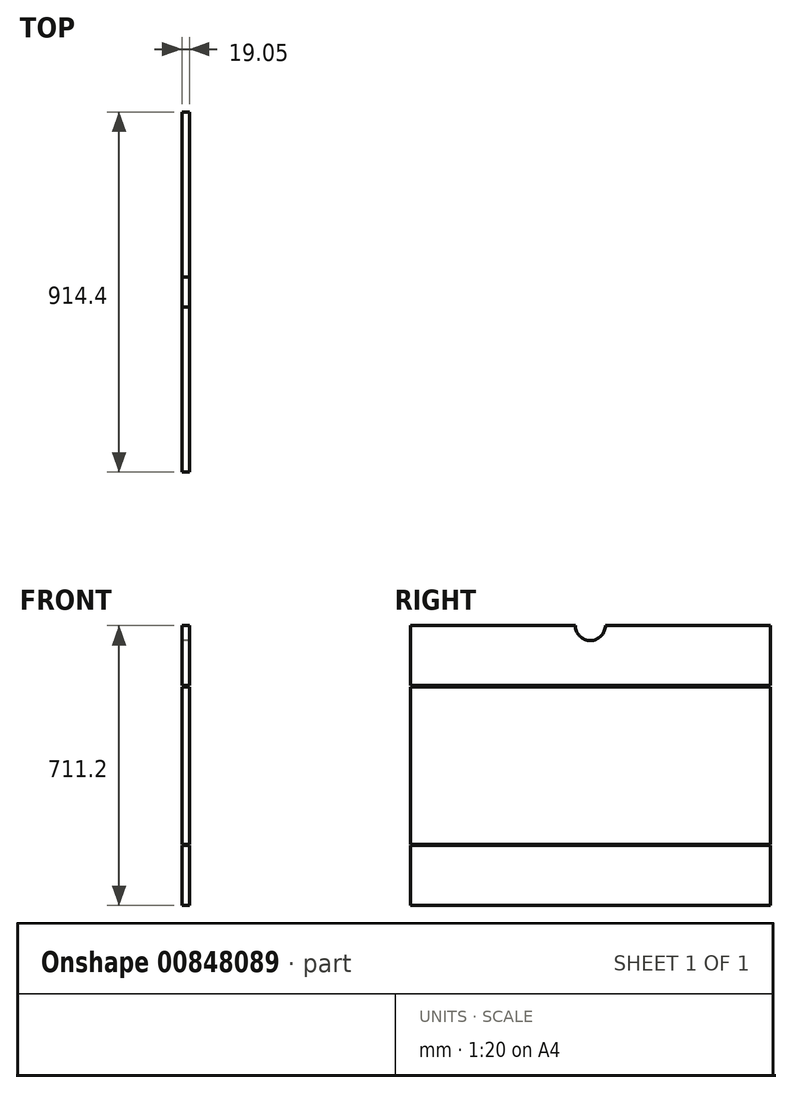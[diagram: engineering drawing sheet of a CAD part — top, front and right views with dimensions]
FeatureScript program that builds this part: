
annotation { "Feature Type Name" : "Feature", "Feature Type Description" : "" }
export const myFeature = defineFeature(function(context is Context, id is Id, definition is map)
    precondition{}
    {
        {
            var Q0;
            Q0=qCreatedBy(makeId("Right.planeOp"),FACE);
            var sketch = newSketch(context, id + "F0", { "sketchPlane" : qUnion([Q0])});
            skLineSegment(sketch, "E0.bottom", {"start": v(457.2, 355.6) * mm, "end": v(-457.2, 355.6) * mm});
            skLineSegment(sketch, "E0.top", {"start": v(457.2, -355.6) * mm, "end": v(-457.2, -355.6) * mm});
            skLineSegment(sketch, "E0.left", {"start": v(457.2, 355.6) * mm, "end": v(457.2, -355.6) * mm});
            skLineSegment(sketch, "E0.right", {"start": v(-457.2, 355.6) * mm, "end": v(-457.2, -355.6) * mm});
            skPoint(sketch, "E0.middle", {"position": v(0, 0) * mm});
            skCircle(sketch, "E1", {"center": v(0, 355.6) * mm, "radius": 38.1 * mm});
            skSolve(sketch);
        }
        {
            var Q0;
            Q0=makeQuery(id+"F0.imprint","IMPRINT",FACE,{"disambiguationData":[TD([[makeQuery(id+"F0.imprint","IMPRINT",EDGE,{"derivedFrom":sQuery(id+"F0.wireOp",EDGE,"E0.top")}),-1.0]])]});
            extrude(context, id + "F1", {"entities" : qUnion([Q0]), "depth" : 19.05 * mm, "offsetDistance" : 25.4 * mm});
        }
        {
            var Q0;
            Q0=makeQuery(id+"F1.opExtrude","CAP_FACE",FACE,{"disambiguationData":[OSD([sQuery(id+"F0.wireOp",EDGE,"E0.bottom"),sQuery(id+"F0.wireOp",EDGE,"E0.top"),sQuery(id+"F0.wireOp",EDGE,"E0.left"),sQuery(id+"F0.wireOp",EDGE,"E0.right"),sQuery(id+"F0.wireOp",EDGE,"E1")])],"isStart":false});
            var sketch = newSketch(context, id + "F2", { "sketchPlane" : qUnion([Q0])});
            skLineSegment(sketch, "E2.bottom", {"start": v(-457.2, 355.6) * mm, "end": v(457.2, 355.6) * mm});
            skLineSegment(sketch, "E2.top", {"start": v(-457.2, 203.2) * mm, "end": v(457.2, 203.2) * mm});
            skLineSegment(sketch, "E2.left", {"start": v(-457.2, 355.6) * mm, "end": v(-457.2, 203.2) * mm});
            skLineSegment(sketch, "E2.right", {"start": v(457.2, 355.6) * mm, "end": v(457.2, 203.2) * mm});
            skLineSegment(sketch, "E3.bottom", {"start": v(-457.2, -355.6) * mm, "end": v(457.2, -355.6) * mm});
            skLineSegment(sketch, "E3.top", {"start": v(-457.2, -203.2) * mm, "end": v(457.2, -203.2) * mm});
            skLineSegment(sketch, "E3.left", {"start": v(-457.2, -355.6) * mm, "end": v(-457.2, -203.2) * mm});
            skLineSegment(sketch, "E3.right", {"start": v(457.2, -355.6) * mm, "end": v(457.2, -203.2) * mm});
            skLineSegment(sketch, "E4.top", {"start": v(-457.2, 200.02) * mm, "end": v(457.2, 200.02) * mm});
            skLineSegment(sketch, "E4.left", {"start": v(-457.2, 203.2) * mm, "end": v(-457.2, 200.02) * mm});
            skLineSegment(sketch, "E4.right", {"start": v(457.2, 203.2) * mm, "end": v(457.2, 200.02) * mm});
            skLineSegment(sketch, "E5.top", {"start": v(-457.2, -200.03) * mm, "end": v(457.2, -200.03) * mm});
            skLineSegment(sketch, "E5.left", {"start": v(-457.2, -203.2) * mm, "end": v(-457.2, -200.03) * mm});
            skLineSegment(sketch, "E5.right", {"start": v(457.2, -203.2) * mm, "end": v(457.2, -200.03) * mm});
            skSolve(sketch);
        }
        {
            var Q0;
            Q0=makeQuery(id+"F2.imprint","IMPRINT",FACE,{"disambiguationData":[TD([[makeQuery(id+"F2.imprint","IMPRINT",EDGE,{"derivedFrom":sQuery(id+"F2.wireOp",EDGE,"E2.top")}),-1.0]])]});
            var Q1;
            Q1=makeQuery(id+"F2.imprint","IMPRINT",FACE,{"disambiguationData":[TD([[makeQuery(id+"F2.imprint","IMPRINT",EDGE,{"derivedFrom":sQuery(id+"F2.wireOp",EDGE,"E3.top")}),1.0]])]});
            extrude(context, id + "F3", {"entities" : qUnion([Q0, Q1]), "operationType" : NewBodyOperationType.REMOVE, "oppositeDirection" : true, "depth" : 25.4 * mm, "offsetDistance" : 25.4 * mm});
        }
    });
